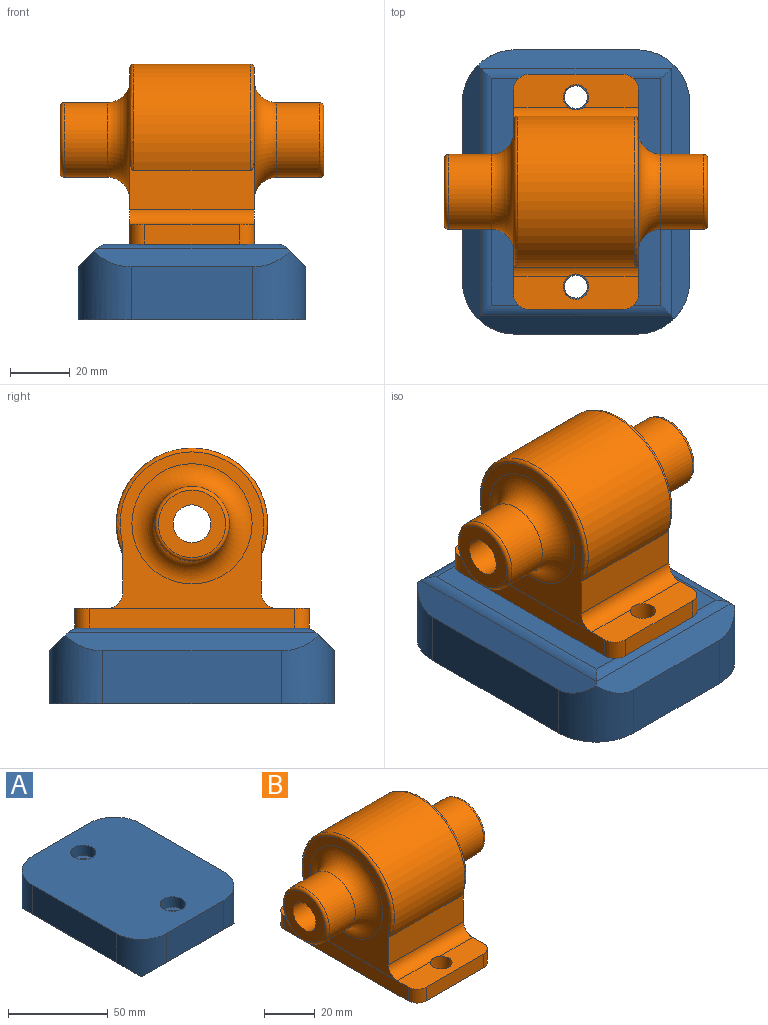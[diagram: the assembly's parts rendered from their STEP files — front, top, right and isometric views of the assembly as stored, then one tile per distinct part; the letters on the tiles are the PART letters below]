
ASSEMBLY  parts=2 mates=1
PART A: 24 faces, bbox 76.2x95.3x25.4 mm
  f0: cylinder r=3.81mm len=19.05mm, axis (0,0,1), area 456mm2, adj f7,f10
  f1: cylinder r=3.81mm len=19.05mm, axis (0,0,1), area 456mm2, adj f7,f9
  f2: plane 95.25x76.2mm, normal (0,0,1), area 6733.3mm2, adj f3,f4,f5,f6,f8,f11,f16,f17
  f3: plane 40.64x17.78mm, normal (0,-1,0), area 722.6mm2, adj f2,f12,f16,f17
  f4: plane 59.69x17.78mm, normal (1,0,0), area 1061.3mm2, adj f2,f13,f16,f19
  f5: plane 40.64x17.78mm, normal (0,1,0), area 722.6mm2, adj f2,f15,f18,f19
  f6: plane 59.69x17.78mm, normal (-1,0,0), area 1061.3mm2, adj f2,f14,f17,f18
  f7: plane 75.8x56.75mm, normal (0,0,-1), area 4210.7mm2, adj f0,f1,f20,f21,f22,f23
  f8: cylinder r=6.35mm len=12.7mm, axis (0,0,1), area 253.4mm2, adj f2,f9
  f9: plane 12.7x12.7mm, normal (0,0,1), area 81.1mm2, adj f1,f8
  f10: plane 12.7x12.7mm, normal (0,0,1), area 81.1mm2, adj f0,f11
  f11: cylinder r=6.35mm len=12.7mm, axis (0,0,1), area 253.4mm2, adj f2,f10
  f12: plane 65.78x6.13mm, normal (0,-0.71,-0.71), area 511.7mm2, adj f3,f13,f14,f16,f17,f20
  f13: plane 84.83x6.13mm, normal (0.71,0,-0.71), area 676.9mm2, adj f4,f12,f15,f16,f19,f22
  f14: plane 84.83x6.13mm, normal (-0.71,0,-0.71), area 676.9mm2, adj f6,f12,f15,f17,f18,f21
  f15: plane 65.78x6.13mm, normal (0,0.71,-0.71), area 511.7mm2, adj f5,f13,f14,f18,f19,f23
  f16: cylinder r=17.78mm len=22.99mm, axis (0,0,-1), area 546.1mm2, adj f2,f3,f4,f12,f13
  f17: cylinder r=17.78mm len=22.99mm, axis (0,0,1), area 546.1mm2, adj f2,f3,f6,f12,f14
  f18: cylinder r=17.78mm len=22.99mm, axis (0,0,-1), area 546.1mm2, adj f2,f5,f6,f14,f15
  f19: cylinder r=17.78mm len=22.99mm, axis (0,0,1), area 546.1mm2, adj f2,f4,f5,f13,f15
  f20: cylinder r=5.08mm len=63.94mm, axis (-1,0,0), area 241.5mm2, adj f7,f12,f21,f22
  f21: cylinder r=5.08mm len=82.99mm, axis (0,1,0), area 317.6mm2, adj f7,f14,f20,f23
  f22: cylinder r=5.08mm len=82.99mm, axis (0,1,0), area 317.6mm2, adj f7,f13,f20,f23
  f23: cylinder r=5.08mm len=63.94mm, axis (-1,0,0), area 241.5mm2, adj f7,f15,f21,f22
PART B: 30 faces, bbox 88.3x78.7x62.6 mm
  f0: plane 78.74x41.91mm, normal (0,0,1), area 810.3mm2, adj f2,f3,f4,f5,f6,f10,f11,f19
  f1: plane 78.74x41.91mm, normal (0,0,-1), area 3164.1mm2, adj f3,f4,f5,f6,f20,f21,f22,f23
  f2: cylinder r=5.08mm len=41.66mm, axis (1,0,0), area 329.6mm2, adj f0,f7,f10,f11,f25
  f3: plane 68.58x6.6mm, normal (1,0,0), area 452.9mm2, adj f0,f1,f20,f23
  f4: plane 31.75x6.6mm, normal (0,1,0), area 209.7mm2, adj f0,f1,f20,f21
  f5: plane 68.58x6.6mm, normal (-1,0,0), area 452.9mm2, adj f0,f1,f21,f22
  f6: plane 31.75x6.6mm, normal (0,-1,0), area 209.7mm2, adj f0,f1,f22,f23
  f7: plane 41.66x16.75mm, normal (0,1,0), area 543.1mm2, adj f2,f8,f10,f11,f28,f29
  f8: cylinder r=25.4mm len=50.8mm, axis (-1,0,0), area 3946.5mm2, adj f7,f9,f28,f29
  f9: plane 41.66x16.75mm, normal (0,-1,0), area 543.1mm2, adj f8,f10,f11,f19,f28,f29
  f10: plane 56.64x52.45mm, normal (1,0,0), area 975.3mm2, adj f0,f2,f7,f9,f16,f19,f29
  f11: plane 56.64x52.45mm, normal (-1,0,0), area 975.3mm2, adj f0,f2,f7,f9,f17,f19,f28
  f12: plane 22.5x22.5mm, normal (-1,0,0), area 271.1mm2, adj f18,f26
  f13: cylinder r=12.52mm len=25.04mm, axis (-1,0,0), area 1134.1mm2, adj f17,f26
  f14: cylinder r=12.52mm len=25.04mm, axis (-1,0,0), area 1134.1mm2, adj f16,f27
  f15: plane 22.5x22.5mm, normal (1,0,0), area 271.1mm2, adj f18,f27
  f16: torus R=20.14mm, axis (1,0,0), area 1150mm2, adj f10,f14
  f17: torus R=20.14mm, axis (1,0,0), area 1150mm2, adj f11,f13
  f18: cylinder r=6.35mm len=88.27mm, axis (1,0,0), area 3521.6mm2, adj f12,f15
  f19: cylinder r=5.08mm len=41.66mm, axis (-1,0,0), area 329.6mm2, adj f0,f9,f10,f11,f24
  f20: cylinder r=5.08mm len=6.6mm, axis (0,0,1), area 52.7mm2, adj f0,f1,f3,f4
  f21: cylinder r=5.08mm len=6.6mm, axis (0,0,-1), area 52.7mm2, adj f0,f1,f4,f5
  f22: cylinder r=5.08mm len=6.6mm, axis (0,0,1), area 52.7mm2, adj f0,f1,f5,f6
  f23: cylinder r=5.08mm len=6.6mm, axis (0,0,-1), area 52.7mm2, adj f0,f1,f3,f6
  f24: cylinder r=4.25mm len=8.51mm, axis (0,0,-1), area 176.5mm2, adj f0,f1,f19
  f25: cylinder r=4.25mm len=8.51mm, axis (0,0,-1), area 176.5mm2, adj f0,f1,f2
  f26: torus R=11.25mm, axis (1,0,0), area 151.2mm2, adj f12,f13
  f27: torus R=11.25mm, axis (1,0,0), area 151.2mm2, adj f14,f15
  f28: torus R=24.13mm, axis (1,0,0), area 193mm2, adj f7,f8,f9,f11
  f29: torus R=24.13mm, axis (1,0,0), area 193mm2, adj f7,f8,f9,f10
PLACE A rot(axis=(0,1,0),180deg) t=(24.68,35.87,-23.13)mm
PLACE B t=(24.68,35.87,2.27)mm
MATE fastened A.f0 <-> B.f25  axis (0,0,1) through (24.68,67.62,2.27)mm
